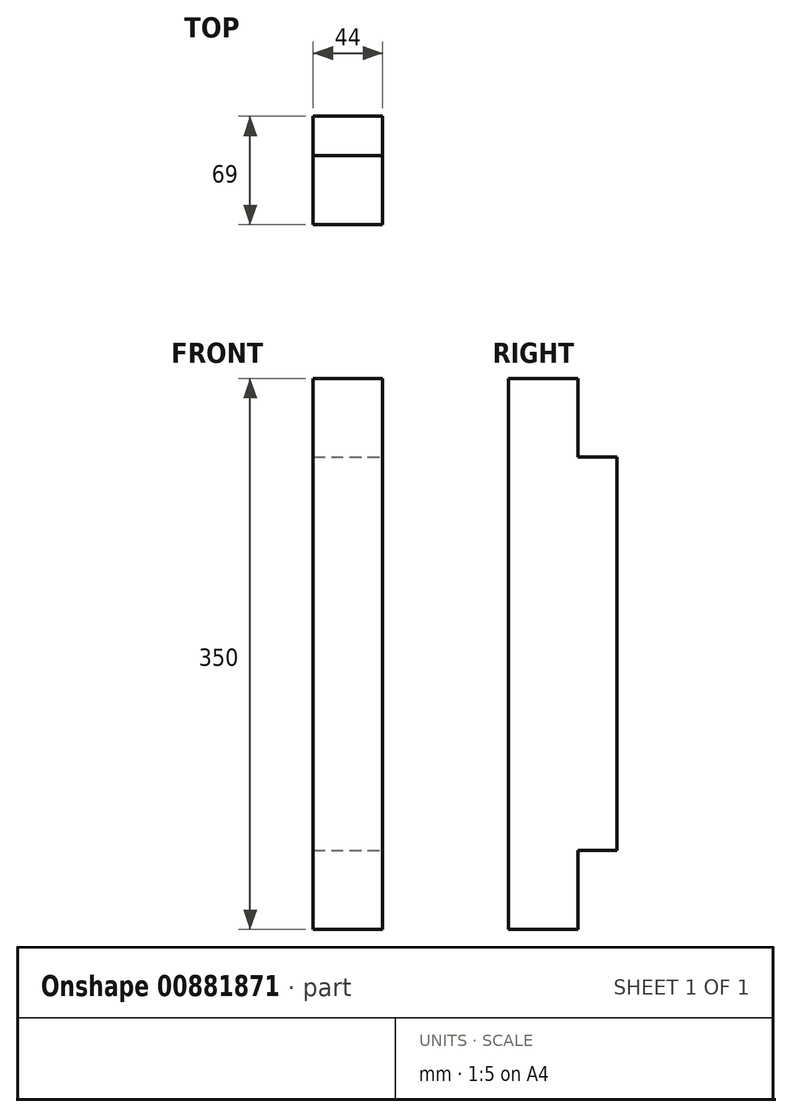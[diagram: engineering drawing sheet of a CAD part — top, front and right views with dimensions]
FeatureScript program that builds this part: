
annotation { "Feature Type Name" : "Feature", "Feature Type Description" : "" }
export const myFeature = defineFeature(function(context is Context, id is Id, definition is map)
    precondition{}
    {
        {
            var Q0;
            Q0=qCreatedBy(makeId("Top.planeOp"),FACE);
            var sketch = newSketch(context, id + "F0", { "sketchPlane" : qUnion([Q0])});
            skLineSegment(sketch, "E0.bottom", {"start": v(22, -34.5) * mm, "end": v(-22, -34.5) * mm});
            skLineSegment(sketch, "E0.top", {"start": v(22, 34.5) * mm, "end": v(-22, 34.5) * mm});
            skLineSegment(sketch, "E0.left", {"start": v(22, -34.5) * mm, "end": v(22, 34.5) * mm});
            skLineSegment(sketch, "E0.right", {"start": v(-22, -34.5) * mm, "end": v(-22, 34.5) * mm});
            skPoint(sketch, "E0.middle", {"position": v(0, 0) * mm});
            skSolve(sketch);
        }
        {
            var Q0;
            Q0=qSketchRegion(id+"F0",true);
            extrude(context, id + "F1", {"entities" : qUnion([Q0]), "depth" : 350 * mm, "offsetDistance" : 25 * mm});
        }
        {
            var Q0;
            Q0=makeQuery(id+"F1.opExtrude","SWEPT_FACE",FACE,{"disambiguationData":[OSD([sQuery(id+"F0.wireOp",EDGE,"E0.left")])]});
            var sketch = newSketch(context, id + "F2", { "sketchPlane" : qUnion([Q0])});
            skLineSegment(sketch, "E1", {"start": v(34.5, 175) * mm, "end": v(-34.5, 175) * mm, "construction": true});
            skLineSegment(sketch, "E2", {"start": v(9.5, 0) * mm, "end": v(9.5, 50) * mm});
            skLineSegment(sketch, "E3", {"start": v(9.5, 50) * mm, "end": v(34.5, 50) * mm});
            skLineSegment(sketch, "E4", {"start": v(9.5, 0) * mm, "end": v(34.5, 0) * mm});
            skLineSegment(sketch, "E5", {"start": v(34.5, 0) * mm, "end": v(34.5, 50) * mm});
            skLineSegment(sketch, "E6.MirrorCS", {"start": v(34.5, 350) * mm, "end": v(34.5, 300) * mm});
            skLineSegment(sketch, "E7.MirrorCS", {"start": v(9.5, 350) * mm, "end": v(34.5, 350) * mm});
            skLineSegment(sketch, "E8.MirrorCS", {"start": v(9.5, 350) * mm, "end": v(9.5, 300) * mm});
            skLineSegment(sketch, "E9.MirrorCS", {"start": v(9.5, 300) * mm, "end": v(34.5, 300) * mm});
            skSolve(sketch);
        }
        {
            var Q0;
            Q0=qSketchRegion(id+"F2",true);
            extrude(context, id + "F3", {"entities" : qUnion([Q0]), "operationType" : NewBodyOperationType.REMOVE, "endBound" : BoundingType.THROUGH_ALL, "oppositeDirection" : true, "depth" : 25 * mm, "offsetDistance" : 25 * mm});
        }
    });
